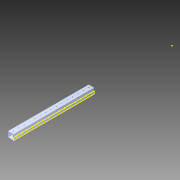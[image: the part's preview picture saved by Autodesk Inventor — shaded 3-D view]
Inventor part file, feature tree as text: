
AUTODESK INVENTOR PART (.ipt)
format: ipt  version: 2014 SP1 (Build 180222100, 222)  size: 1,248,768 bytes
history: native  units: in
note: dims shown in document units (in); Inventor stores cm internally (conversion verified against a paired STEP export)
features: sketch x2, pattern_circular x1, other x1, plane x1, extrude x1, imported_body x1
ambient origin geometry x8: Origin, YZ Plane, XZ Plane, XY Plane, X Axis, Y Axis, Z Axis, Center Point
bodies: Body1 (feature_tree)
feature tree (7):
  pattern_circular  "CirPattern2"
  other  "217-3426-STEP1"
  plane  "Work Plane1"
  extrude  "Extrusion1"  Depth=3937.0079in TaperAngle=0.0deg
  sketch  "Sketch3"
  imported_body  "Base1"
  sketch  "Sketch1"  dims[d0=-15.0in d1=3937.0079in d2=0.0in]
